# Revit family: Platek_Blend Applique 360
name_source: partatom
category: Apparecchi per illuminazione
revit_build: Autodesk Revit 2017 (Build: 20160225_1515(x64)
units: mm (PartAtom-declared; Revit-internal decimal feet)

## family parameters
Basato su piano di lavoro = No
Condiviso = No
Punto di calcolo locali = No
Quota connettore circolare = Usa diametro
Sempre verticale = Sì
Sorgente d'illuminazione = Sì
Taglio con vuoti quando caricato = No
Tipo di parte = Normale

## types (1)
- 1610616_13,5W_LED_3000K
    Angolo inclinazione = 90.00°
    Body = PLK_06_Grey
    CRI = >80
    Carico apparente = 0 VA
    Codice assieme = 1610616.02(White); 1610616.06(Grey); 1610616.01(Black); 1610616.08(Anthracite); 1610616.01(Black); 1610616.07(Corten); 1610616.09(Bronze)
    Colour Temperature = 3000 K
    Commenti sul tipo = Facades, Wall
    Descrizione = Outdoor Lighting, Wall mounted
    Diffuse Type = PMMA
    Dimmable = On request
    Energy Efficiency Rating = A/A+/A++
    File diagramma fotometrico = 1610616.IES
    Filtro dei colori = 16777215
    Frequency = 50/60 Hz
    IK Rating = IK05
    IP Rating = IP65
    Immagine tipo = blend_applique_360.jpg
    Insulation Class = 1
    LED Protection = Surge protection included
    Lampada = LED
    Light Source = PLK_Light Source
    Luminaire Luminous Flux = 1060 lm
    Luminaire Luminous Intensity = 301 cd
    Luminaire Wattage = 14 W
    Modello = Blend 360 Applique
    Mounting Type = Wall
    Nota chiave = Other LED colors available on request
    PLATEK Article Code = 1610616
    Part of body = PLK_Part of body
    Power Supply Unit = Included
    Product Dimension = L160mm x L160mm x 71,5mm
    Product Documentation Link = http://www.platek.eu
    Product Page URL = http://www.platek.eu
    Produttore = PLATEK SRL
    Supply Voltage = 230 V
    Supply Voltage Max = 240 V
    Supply Voltage Min = 220 V
    URL = www.platek.eu
    Variazione temperatura colore lampada con luminosità attenuata = <Nessuno>

## geometry (parser evidence)
native form markers: Blend x5
no freeform markers — native parametric forms only
